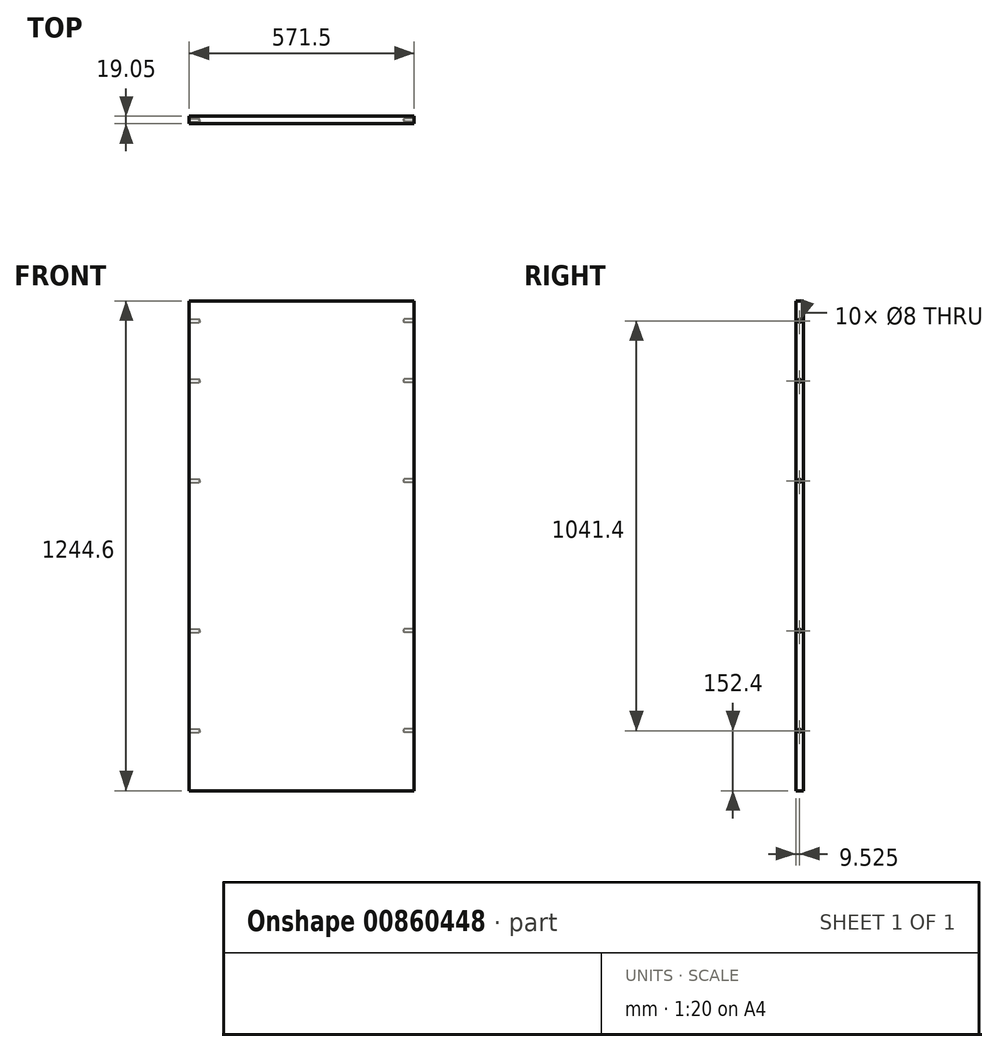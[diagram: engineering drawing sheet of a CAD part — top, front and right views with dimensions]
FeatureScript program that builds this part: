
annotation { "Feature Type Name" : "Feature", "Feature Type Description" : "" }
export const myFeature = defineFeature(function(context is Context, id is Id, definition is map)
    precondition{}
    {
        {
            var Q0;
            Q0=qCreatedBy(makeId("Front.planeOp"),FACE);
            var sketch = newSketch(context, id + "F0", { "sketchPlane" : qUnion([Q0])});
            skLineSegment(sketch, "E0.bottom", {"start": v(285.75, 622.3) * mm, "end": v(-285.75, 622.3) * mm});
            skLineSegment(sketch, "E0.top", {"start": v(285.75, -622.3) * mm, "end": v(-285.75, -622.3) * mm});
            skLineSegment(sketch, "E0.left", {"start": v(285.75, 622.3) * mm, "end": v(285.75, -622.3) * mm});
            skLineSegment(sketch, "E0.right", {"start": v(-285.75, 622.3) * mm, "end": v(-285.75, -622.3) * mm});
            skPoint(sketch, "E0.middle", {"position": v(0, 0) * mm});
            skSolve(sketch);
        }
        {
            var Q0;
            Q0=makeQuery(id+"F0.imprint","IMPRINT",FACE,{"disambiguationData":[TD([[makeQuery(id+"F0.imprint","IMPRINT",EDGE,{"derivedFrom":sQuery(id+"F0.wireOp",EDGE,"E0.bottom")}),1.0]])]});
            extrude(context, id + "F1", {"entities" : qUnion([Q0]), "depth" : 19.05 * mm, "offsetDistance" : 25.4 * mm});
        }
        {
            var Q0;
            Q0=makeQuery(id+"F1.opExtrude","SWEPT_FACE",FACE,{"disambiguationData":[OSD([sQuery(id+"F0.wireOp",EDGE,"E0.left")])]});
            var sketch = newSketch(context, id + "F2", { "sketchPlane" : qUnion([Q0])});
            skLineSegment(sketch, "E1", {"start": v(-9.53, 622.3) * mm, "end": v(-9.53, 571.5) * mm});
            skLineSegment(sketch, "E2", {"start": v(-9.53, 622.3) * mm, "end": v(-9.53, 419.1) * mm});
            skLineSegment(sketch, "E3", {"start": v(-9.53, 622.3) * mm, "end": v(-9.53, 165.1) * mm});
            skLineSegment(sketch, "E4", {"start": v(-9.53, -622.3) * mm, "end": v(-9.53, -469.9) * mm});
            skLineSegment(sketch, "E5", {"start": v(-9.53, -622.3) * mm, "end": v(-9.53, -215.9) * mm});
            skPoint(sketch, "E6", {"position": v(-9.53, 571.5) * mm});
            skPoint(sketch, "E7", {"position": v(-9.52, 419.1) * mm});
            skPoint(sketch, "E8", {"position": v(-9.52, 165.1) * mm});
            skPoint(sketch, "E9", {"position": v(-9.53, -215.9) * mm});
            skPoint(sketch, "E10", {"position": v(-9.53, -469.9) * mm});
            skSolve(sketch);
        }
        {
            var Q0;
            Q0=sQuery(id+"F2.wireOp",VERTEX,"E6");
            var Q1;
            Q1=sQuery(id+"F2.wireOp",VERTEX,"E7");
            var Q2;
            Q2=sQuery(id+"F2.wireOp",VERTEX,"E8");
            var Q3;
            Q3=sQuery(id+"F2.wireOp",VERTEX,"E9");
            var Q4;
            Q4=sQuery(id+"F2.wireOp",VERTEX,"E10");
            var Q5;
            Q5=makeQuery(id+"F1.opExtrude","SWEPT_BODY",BODY,{"disambiguationData":[OSD([sQuery(id+"F0.wireOp",EDGE,"E0.bottom"),sQuery(id+"F0.wireOp",EDGE,"E0.top"),sQuery(id+"F0.wireOp",EDGE,"E0.left"),sQuery(id+"F0.wireOp",EDGE,"E0.right")])]});
            hole(context, id + "F3", {"style" : HoleStyle.SIMPLE, "endStyle" : HoleEndStyle.BLIND, "holeDiameter" : 8 * mm, "majorDiameter" : 6.35 * mm, "holeDepth" : 25.4 * mm, "isTappedThrough" : true, "tappedDepth" : 12.7 * mm, "tapClearance" : 3, "locations" : qUnion([Q0, Q1, Q2, Q3, Q4]), "scope" : qUnion([Q5]), "startStyle" : HoleStartStyle.SKETCH});
        }
        {
            var Q0;
            Q0=makeQuery(id+"F1.opExtrude","SWEPT_FACE",FACE,{"disambiguationData":[OSD([sQuery(id+"F0.wireOp",EDGE,"E0.right")])]});
            var sketch = newSketch(context, id + "F4", { "sketchPlane" : qUnion([Q0])});
            skLineSegment(sketch, "E11", {"start": v(9.53, 622.3) * mm, "end": v(9.53, 571.5) * mm});
            skLineSegment(sketch, "E12", {"start": v(9.53, 622.3) * mm, "end": v(9.53, 419.1) * mm});
            skLineSegment(sketch, "E13", {"start": v(9.53, 622.3) * mm, "end": v(9.53, 165.1) * mm});
            skLineSegment(sketch, "E14", {"start": v(9.53, -622.3) * mm, "end": v(9.53, -469.9) * mm});
            skLineSegment(sketch, "E15", {"start": v(9.53, -622.3) * mm, "end": v(9.53, -215.9) * mm});
            skPoint(sketch, "E16", {"position": v(9.53, 571.5) * mm});
            skPoint(sketch, "E17", {"position": v(9.53, 419.1) * mm});
            skPoint(sketch, "E18", {"position": v(9.53, 165.1) * mm});
            skPoint(sketch, "E19", {"position": v(9.52, -215.9) * mm});
            skPoint(sketch, "E20", {"position": v(9.53, -469.9) * mm});
            skSolve(sketch);
        }
        {
            var Q0;
            Q0=sQuery(id+"F4.wireOp",VERTEX,"E16");
            var Q1;
            Q1=sQuery(id+"F4.wireOp",VERTEX,"E17");
            var Q2;
            Q2=sQuery(id+"F4.wireOp",VERTEX,"E13.end");
            var Q3;
            Q3=sQuery(id+"F4.wireOp",VERTEX,"E19");
            var Q4;
            Q4=sQuery(id+"F4.wireOp",VERTEX,"E20");
            var Q5;
            Q5=makeQuery(id+"F1.opExtrude","SWEPT_BODY",BODY,{"disambiguationData":[OSD([sQuery(id+"F0.wireOp",EDGE,"E0.bottom"),sQuery(id+"F0.wireOp",EDGE,"E0.top"),sQuery(id+"F0.wireOp",EDGE,"E0.left"),sQuery(id+"F0.wireOp",EDGE,"E0.right")])]});
            hole(context, id + "F5", {"style" : HoleStyle.SIMPLE, "endStyle" : HoleEndStyle.BLIND, "holeDiameter" : 8 * mm, "majorDiameter" : 6.35 * mm, "holeDepth" : 25.4 * mm, "isTappedThrough" : true, "tappedDepth" : 12.7 * mm, "tapClearance" : 3, "locations" : qUnion([Q0, Q1, Q2, Q3, Q4]), "scope" : qUnion([Q5]), "startStyle" : HoleStartStyle.SKETCH});
        }
    });
